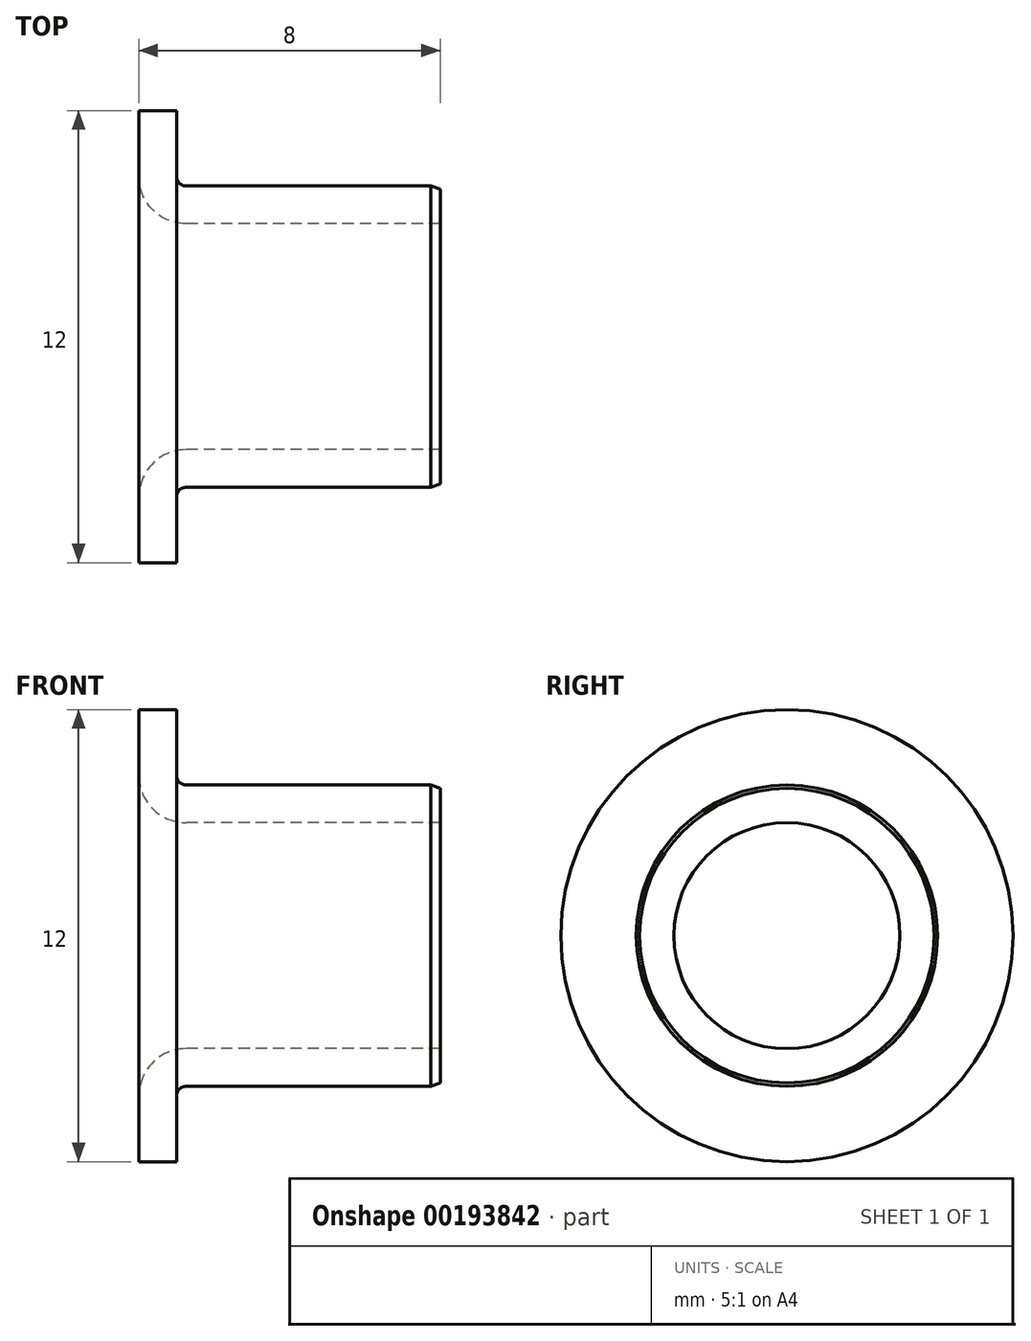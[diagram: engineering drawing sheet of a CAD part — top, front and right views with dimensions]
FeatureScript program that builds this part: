
annotation { "Feature Type Name" : "Feature", "Feature Type Description" : "" }
export const myFeature = defineFeature(function(context is Context, id is Id, definition is map)
    precondition{}
    {
        {
            var Q0;
            Q0=qCreatedBy(makeId("Front.planeOp"),FACE);
            var sketch = newSketch(context, id + "F0", { "sketchPlane" : qUnion([Q0])});
            skLineSegment(sketch, "E0", {"start": v(-0.57, 3) * mm, "end": v(6.18, 3) * mm});
            skLineSegment(sketch, "E1", {"start": v(6.18, 3) * mm, "end": v(6.18, 3.9) * mm});
            skLineSegment(sketch, "E2", {"start": v(5.93, 4) * mm, "end": v(-0.57, 4) * mm});
            skLineSegment(sketch, "E3", {"start": v(-0.82, 4.25) * mm, "end": v(-0.82, 6) * mm});
            skLineSegment(sketch, "E4", {"start": v(-0.82, 6) * mm, "end": v(-1.82, 6) * mm});
            skLineSegment(sketch, "E5", {"start": v(-5.16, 0) * mm, "end": v(3.83, 0) * mm, "construction": true});
            skLineSegment(sketch, "E6", {"start": v(-1.82, 6) * mm, "end": v(-1.82, 4.25) * mm});
            skArc(sketch, "E7", {"start": v(-0.82, 4.25) * mm, "mid": v(-0.74, 4.07) * mm, "end": v(-0.57, 4) * mm});
            skArc(sketch, "E8", {"start": v(-1.82, 4.25) * mm, "mid": v(-1.45, 3.37) * mm, "end": v(-0.57, 3) * mm});
            skLineSegment(sketch, "E9", {"start": v(5.93, 4) * mm, "end": v(6.18, 3.9) * mm});
            skSolve(sketch);
        }
        {
            var Q0;
            Q0=makeQuery(id+"F0.imprint","IMPRINT",FACE,{"disambiguationData":[TD([[makeQuery(id+"F0.imprint","IMPRINT",EDGE,{"derivedFrom":sQuery(id+"F0.wireOp",EDGE,"E0")}),1.0]])]});
            var Q1;
            Q1=sQuery(id+"F0.wireOp",EDGE,"E5");
            revolve(context, id + "F1", {"entities" : qUnion([Q0]), "axis" : qUnion([Q1]), "revolveType" : RevolveType.FULL});
        }
    });
